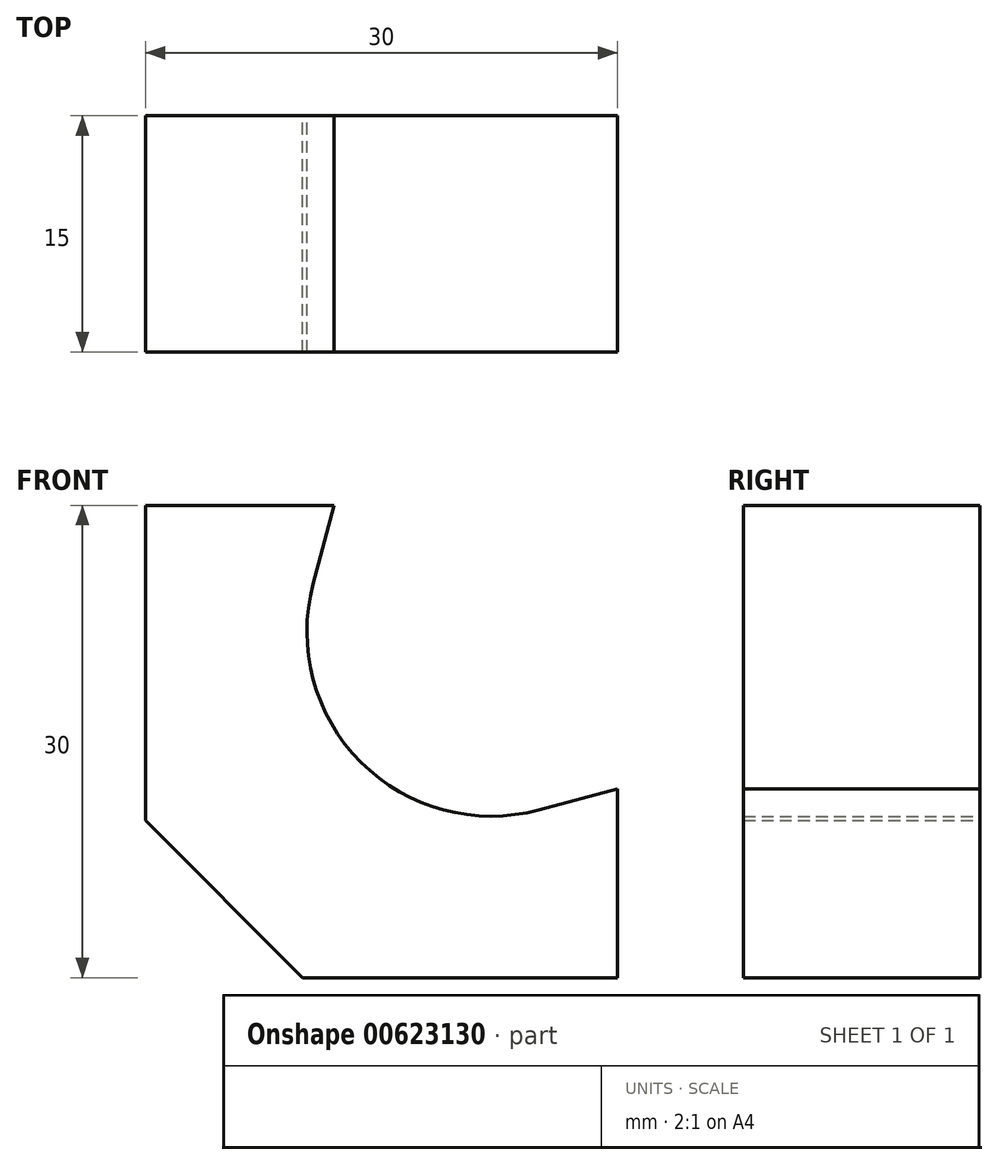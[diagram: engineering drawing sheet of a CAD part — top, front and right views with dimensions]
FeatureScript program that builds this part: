
annotation { "Feature Type Name" : "Feature", "Feature Type Description" : "" }
export const myFeature = defineFeature(function(context is Context, id is Id, definition is map)
    precondition{}
    {
        {
            var Q0;
            Q0=qCreatedBy(makeId("Front.planeOp"),FACE);
            var sketch = newSketch(context, id + "F0", { "sketchPlane" : qUnion([Q0])});
            skLineSegment(sketch, "E0", {"start": v(0, 30) * mm, "end": v(0, 10) * mm});
            skLineSegment(sketch, "E1", {"start": v(0, 10) * mm, "end": v(10, 0) * mm});
            skLineSegment(sketch, "E2", {"start": v(10, 0) * mm, "end": v(30, 0) * mm});
            skLineSegment(sketch, "E3", {"start": v(30, 0) * mm, "end": v(30, 12) * mm});
            skLineSegment(sketch, "E4", {"start": v(0, 30) * mm, "end": v(12, 30) * mm});
            skLineSegment(sketch, "E5", {"start": v(12, 30) * mm, "end": v(10.66, 25) * mm});
            skLineSegment(sketch, "E6", {"start": v(30, 12) * mm, "end": v(25, 10.66) * mm});
            skArc(sketch, "E7", {"start": v(10.66, 25) * mm, "mid": v(13.7, 13.7) * mm, "end": v(25, 10.66) * mm});
            skSolve(sketch);
        }
        {
            var Q0;
            Q0=makeQuery(id+"F0.imprint","IMPRINT",FACE,{"disambiguationData":[TD([[makeQuery(id+"F0.imprint","IMPRINT",EDGE,{"derivedFrom":sQuery(id+"F0.wireOp",EDGE,"E0")}),1.0]])]});
            extrude(context, id + "F1", {"entities" : qUnion([Q0]), "endBound" : BoundingType.SYMMETRIC, "depth" : 15 * mm, "offsetDistance" : 25 * mm});
        }
    });
